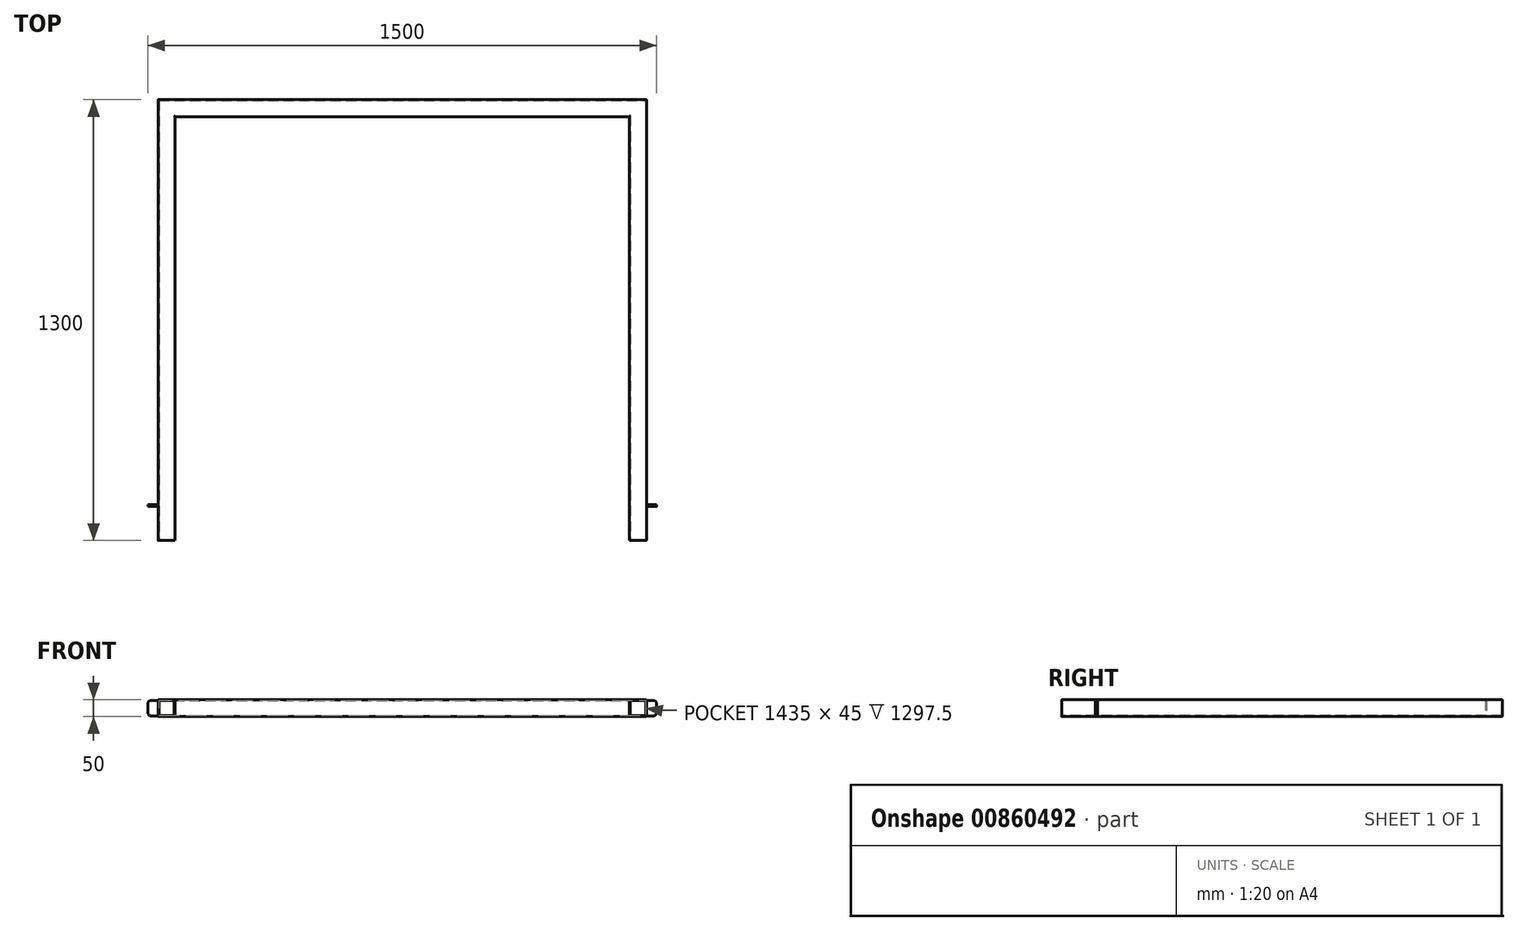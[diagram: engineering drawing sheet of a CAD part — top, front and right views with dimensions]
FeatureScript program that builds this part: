
annotation { "Feature Type Name" : "Feature", "Feature Type Description" : "" }
export const myFeature = defineFeature(function(context is Context, id is Id, definition is map)
    precondition{}
    {
        {
            var Q0;
            Q0=qCreatedBy(makeId("Top.planeOp"),FACE);
            var sketch = newSketch(context, id + "F0", { "sketchPlane" : qUnion([Q0])});
            skLineSegment(sketch, "E0.bottom", {"start": v(720, 675) * mm, "end": v(-720, 675) * mm});
            skLineSegment(sketch, "E0.left", {"start": v(720, 675) * mm, "end": v(720, -625) * mm});
            skLineSegment(sketch, "E0.right", {"start": v(-720, 675) * mm, "end": v(-720, -625) * mm});
            skPoint(sketch, "E0.middle", {"position": v(0, 0) * mm});
            skLineSegment(sketch, "E1.bottom", {"start": v(670, 625) * mm, "end": v(-670, 625) * mm});
            skLineSegment(sketch, "E1.left", {"start": v(670, 625) * mm, "end": v(670, -625) * mm});
            skLineSegment(sketch, "E1.right", {"start": v(-670, 625) * mm, "end": v(-670, -625) * mm});
            skLineSegment(sketch, "E2", {"start": v(-670, -625) * mm, "end": v(-720, -625) * mm});
            skLineSegment(sketch, "E3", {"start": v(670, -625) * mm, "end": v(720, -625) * mm});
            skSolve(sketch);
        }
        {
            var Q0;
            Q0=qSketchRegion(id+"F0",true);
            extrude(context, id + "F1", {"entities" : qUnion([Q0]), "depth" : 50 * mm, "offsetDistance" : 25 * mm});
        }
        {
            var Q0;
            Q0=makeQuery(id+"F1.opExtrude","CAP_EDGE",EDGE,{"disambiguationData":[OSD([sQuery(id+"F0.wireOp",EDGE,"E0.right")])],"isStart":false});
            var Q1;
            Q1=makeQuery(id+"F1.opExtrude","CAP_EDGE",EDGE,{"disambiguationData":[OSD([sQuery(id+"F0.wireOp",EDGE,"E1.right")])],"isStart":false});
            var Q2;
            Q2=makeQuery(id+"F1.opExtrude","CAP_EDGE",EDGE,{"disambiguationData":[OSD([sQuery(id+"F0.wireOp",EDGE,"E0.right")])],"isStart":true});
            var Q3;
            Q3=makeQuery(id+"F1.opExtrude","CAP_EDGE",EDGE,{"disambiguationData":[OSD([sQuery(id+"F0.wireOp",EDGE,"E1.right")])],"isStart":true});
            var Q4;
            Q4=makeQuery(id+"F1.opExtrude","CAP_EDGE",EDGE,{"disambiguationData":[OSD([sQuery(id+"F0.wireOp",EDGE,"E1.left")])],"isStart":false});
            var Q5;
            Q5=makeQuery(id+"F1.opExtrude","CAP_EDGE",EDGE,{"disambiguationData":[OSD([sQuery(id+"F0.wireOp",EDGE,"E0.left")])],"isStart":false});
            var Q6;
            Q6=makeQuery(id+"F1.opExtrude","CAP_EDGE",EDGE,{"disambiguationData":[OSD([sQuery(id+"F0.wireOp",EDGE,"E1.left")])],"isStart":true});
            var Q7;
            Q7=makeQuery(id+"F1.opExtrude","CAP_EDGE",EDGE,{"disambiguationData":[OSD([sQuery(id+"F0.wireOp",EDGE,"E0.left")])],"isStart":true});
            var Q8;
            Q8=makeQuery(id+"F1.opExtrude","CAP_EDGE",EDGE,{"disambiguationData":[OSD([sQuery(id+"F0.wireOp",EDGE,"E0.bottom")])],"isStart":true});
            var Q9;
            Q9=makeQuery(id+"F1.opExtrude","CAP_EDGE",EDGE,{"disambiguationData":[OSD([sQuery(id+"F0.wireOp",EDGE,"E0.bottom")])],"isStart":false});
            var Q10;
            Q10=makeQuery(id+"F1.opExtrude","CAP_EDGE",EDGE,{"disambiguationData":[OSD([sQuery(id+"F0.wireOp",EDGE,"E1.bottom")])],"isStart":true});
            var Q11;
            Q11=makeQuery(id+"F1.opExtrude","CAP_EDGE",EDGE,{"disambiguationData":[OSD([sQuery(id+"F0.wireOp",EDGE,"E1.bottom")])],"isStart":false});
            fillet(context, id + "F2", {"entities" : qUnion([Q0, Q1, Q2, Q3, Q4, Q5, Q6, Q7, Q8, Q9, Q10, Q11]), "radius" : 2 * mm, "tangentPropagation" : true, "allowEdgeOverflow" : false});
        }
        {
            var Q0;
            Q0=makeQuery(id+"F1.opExtrude","SWEPT_FACE",FACE,{"disambiguationData":[OSD([sQuery(id+"F0.wireOp",EDGE,"E2")])]});
            var Q1;
            Q1=makeQuery(id+"F1.opExtrude","SWEPT_FACE",FACE,{"disambiguationData":[OSD([sQuery(id+"F0.wireOp",EDGE,"E3")])]});
            shell(context, id + "F3", {"entities" : qUnion([Q0, Q1]), "thickness" : 2.5 * mm});
        }
        {
            var Q0;
            Q0=makeQuery(id+"F1.opExtrude","SWEPT_FACE",FACE,{"disambiguationData":[OSD([sQuery(id+"F0.wireOp",EDGE,"E0.right")])]});
            var sketch = newSketch(context, id + "F4", { "sketchPlane" : qUnion([Q0])});
            skLineSegment(sketch, "E4.bottom", {"start": v(519, 48) * mm, "end": v(525, 48) * mm});
            skLineSegment(sketch, "E4.top", {"start": v(519, 2) * mm, "end": v(525, 2) * mm});
            skLineSegment(sketch, "E4.left", {"start": v(519, 48) * mm, "end": v(519, 2) * mm});
            skLineSegment(sketch, "E4.right", {"start": v(525, 48) * mm, "end": v(525, 2) * mm});
            skSolve(sketch);
        }
        {
            var Q0;
            Q0 = qSketchRegion(id + "F4", true);
            extrude(context, id + "F5", {"entities" : qUnion([Q0]), "depth" : 30 * mm, "offsetDistance" : 25 * mm});
        }
        {
            var Q0;
            Q0=makeQuery(id+"F5.opExtrude","CAP_EDGE",EDGE,{"disambiguationData":[OSD([sQuery(id+"F4.wireOp",EDGE,"E4.bottom")])],"isStart":false});
            var Q1;
            Q1=makeQuery(id+"F5.opExtrude","CAP_EDGE",EDGE,{"disambiguationData":[OSD([sQuery(id+"F4.wireOp",EDGE,"E4.top")])],"isStart":false});
            fillet(context, id + "F6", {"entities" : qUnion([Q0, Q1]), "radius" : 10 * mm, "tangentPropagation" : true, "allowEdgeOverflow" : false});
        }
        {
            var Q0;
            Q0=makeQuery(id+"F5.opExtrude","SWEPT_BODY",BODY,{"disambiguationData":[OSD([sQuery(id+"F4.wireOp",EDGE,"E4.bottom"),sQuery(id+"F4.wireOp",EDGE,"E4.top"),sQuery(id+"F4.wireOp",EDGE,"E4.left"),sQuery(id+"F4.wireOp",EDGE,"E4.right")])]});
            var Q1;
            Q1=qCreatedBy(makeId("Right.planeOp"),FACE);
            mirror(context, id + "F7", {"operationType" : NewBodyOperationType.ADD, "entities" : qUnion([Q0]), "mirrorPlane" : qUnion([Q1])});
        }
    });
